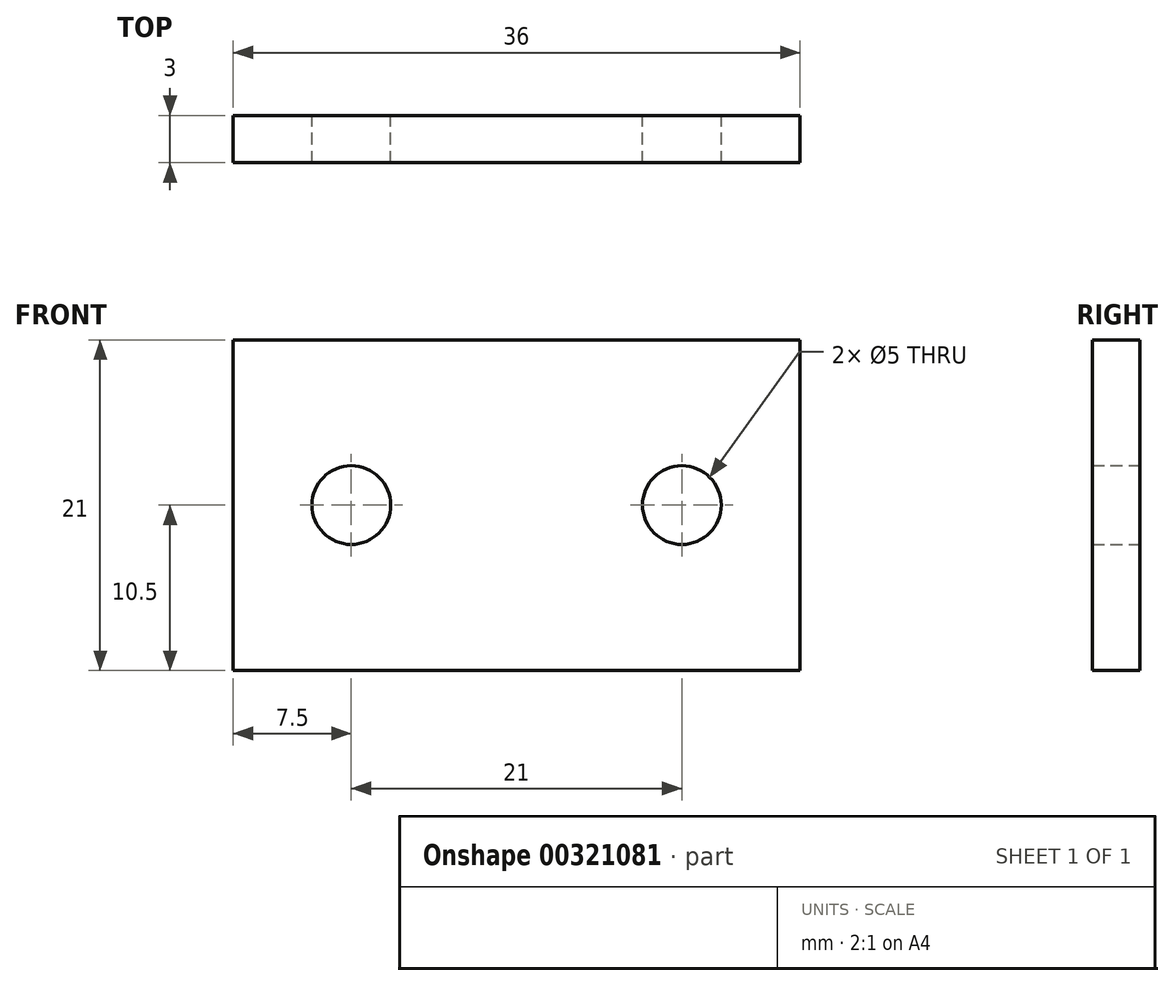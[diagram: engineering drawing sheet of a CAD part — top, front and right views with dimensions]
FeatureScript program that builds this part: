
annotation { "Feature Type Name" : "Feature", "Feature Type Description" : "" }
export const myFeature = defineFeature(function(context is Context, id is Id, definition is map)
    precondition{}
    {
        {
            var Q0;
            Q0=qCreatedBy(makeId("Front.planeOp"),FACE);
            var sketch = newSketch(context, id + "F0", { "sketchPlane" : qUnion([Q0])});
            skLineSegment(sketch, "E0.bottom", {"start": v(18, 10.5) * mm, "end": v(-18, 10.5) * mm});
            skLineSegment(sketch, "E0.top", {"start": v(18, -10.5) * mm, "end": v(-18, -10.5) * mm});
            skLineSegment(sketch, "E0.left", {"start": v(18, 10.5) * mm, "end": v(18, -10.5) * mm});
            skLineSegment(sketch, "E0.right", {"start": v(-18, 10.5) * mm, "end": v(-18, -10.5) * mm});
            skPoint(sketch, "E0.middle", {"position": v(0, 0) * mm});
            skCircle(sketch, "E1", {"center": v(-10.5, 0) * mm, "radius": 2.5 * mm});
            skCircle(sketch, "E2", {"center": v(10.5, 0) * mm, "radius": 2.5 * mm});
            skSolve(sketch);
        }
        {
            var Q0;
            Q0 = qSketchRegion(id + "F0", true);
            extrude(context, id + "F1", {"entities" : qUnion([Q0]), "depth" : 3 * mm});
        }
    });
